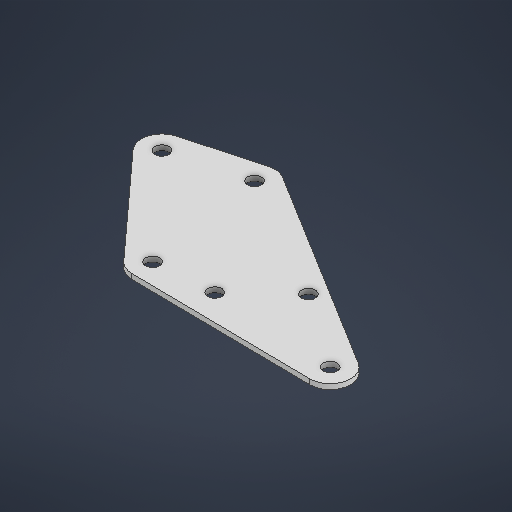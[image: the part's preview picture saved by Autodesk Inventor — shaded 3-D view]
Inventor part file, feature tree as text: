
AUTODESK INVENTOR PART (.ipt)
format: ipt  version: 2025.2 (Build 292293000, 293)  size: 198,144 bytes
history: native  units: in
note: dims shown in document units (in); Inventor stores cm internally (conversion verified against a paired STEP export)
features: extrude x1, sketch x1
ambient origin geometry x8: Origin, YZ Plane, XZ Plane, XY Plane, X Axis, Y Axis, Z Axis, Center Point
bodies: Solid1 (feature_tree)
feature tree (2):
  extrude  "Extrusion1"  [1 undecoded]
  sketch  "Sketch1"  dims[d8=0.0625in d9=0.0in]
note: 1 required parameter value undecoded (feature->parameter linkage not recoverable at this tier; creation-order binding heuristic only, values carry confidence <= 0.55)
